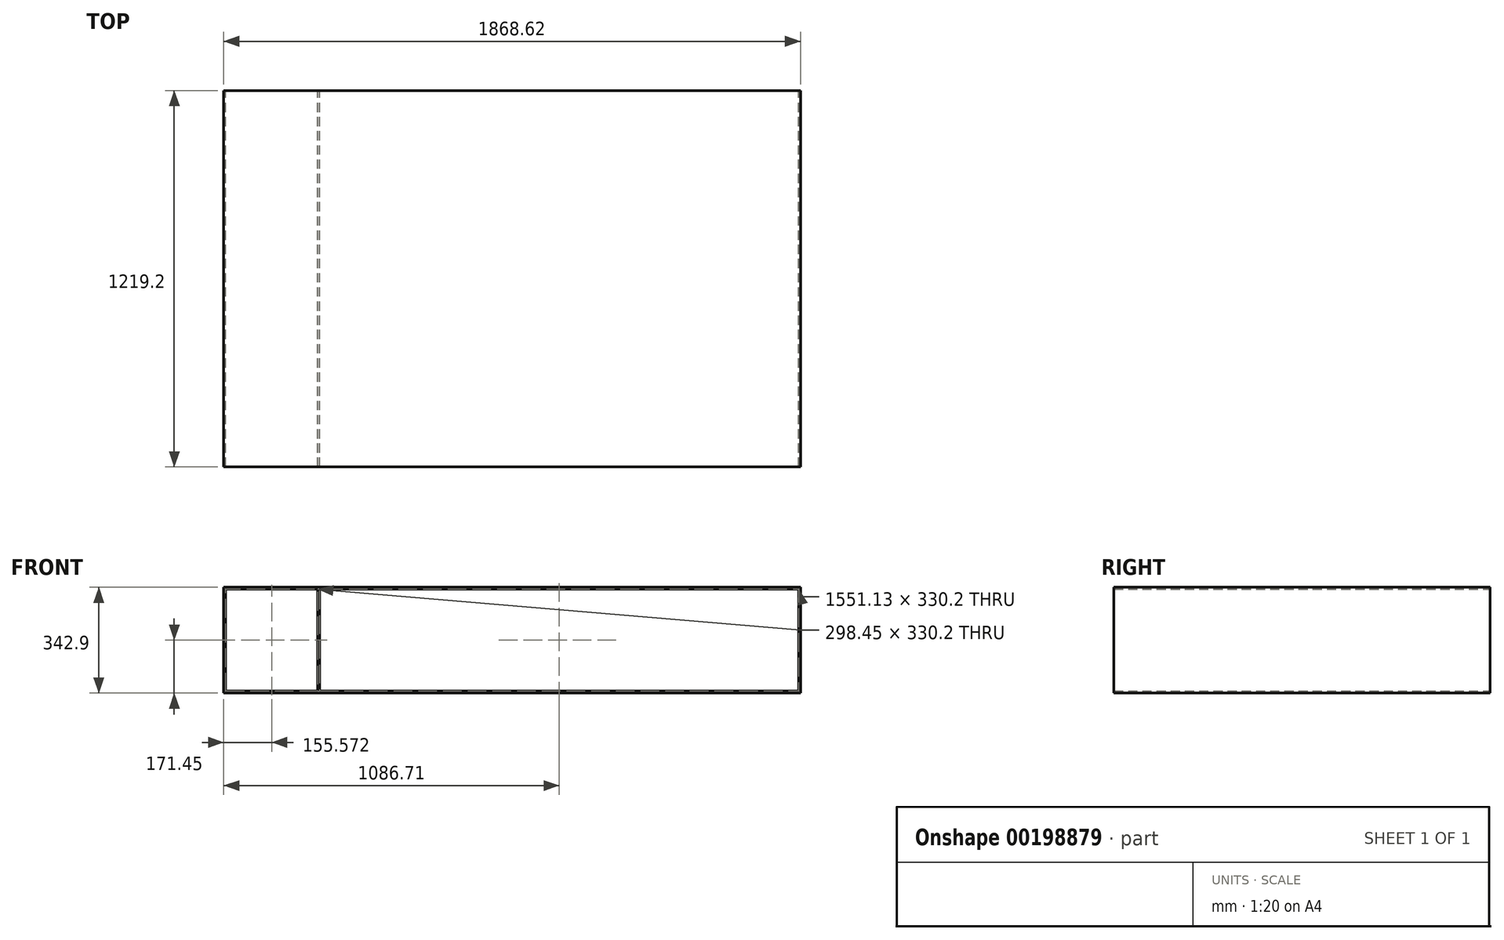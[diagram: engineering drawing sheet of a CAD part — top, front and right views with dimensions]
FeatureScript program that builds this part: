
annotation { "Feature Type Name" : "Feature", "Feature Type Description" : "" }
export const myFeature = defineFeature(function(context is Context, id is Id, definition is map)
    precondition{}
    {
        {
            var Q0;
            Q0=qCreatedBy(makeId("Front.planeOp"),FACE);
            var sketch = newSketch(context, id + "F0", { "sketchPlane" : qUnion([Q0])});
            skLineSegment(sketch, "E0.bottom", {"start": v(-927.96, 0) * mm, "end": v(-629.51, 0) * mm});
            skLineSegment(sketch, "E0.top", {"start": v(-927.96, 330.2) * mm, "end": v(-629.51, 330.2) * mm});
            skLineSegment(sketch, "E0.left", {"start": v(-927.96, 0) * mm, "end": v(-927.96, 330.2) * mm});
            skLineSegment(sketch, "E0.right", {"start": v(927.96, 0) * mm, "end": v(927.96, 330.2) * mm});
            skLineSegment(sketch, "E1.bottom", {"start": v(-934.31, -6.35) * mm, "end": v(934.31, -6.35) * mm});
            skLineSegment(sketch, "E1.top", {"start": v(-934.31, 336.55) * mm, "end": v(934.31, 336.55) * mm});
            skLineSegment(sketch, "E1.left", {"start": v(-934.31, -6.35) * mm, "end": v(-934.31, 336.55) * mm});
            skLineSegment(sketch, "E1.right", {"start": v(934.31, -6.35) * mm, "end": v(934.31, 336.55) * mm});
            skLineSegment(sketch, "E2", {"start": v(0, 336.55) * mm, "end": v(0, 330.2) * mm, "construction": true});
            skLineSegment(sketch, "E3", {"start": v(927.96, 165.1) * mm, "end": v(934.31, 165.1) * mm, "construction": true});
            skLineSegment(sketch, "E4", {"start": v(-629.51, 330.2) * mm, "end": v(-629.51, 0) * mm});
            skLineSegment(sketch, "E5", {"start": v(-623.16, 330.2) * mm, "end": v(-623.16, 0) * mm});
            skLineSegment(sketch, "E6.trimOffspring", {"start": v(-623.16, 330.2) * mm, "end": v(927.96, 330.2) * mm});
            skLineSegment(sketch, "E7.trimOffspring", {"start": v(-623.16, 0) * mm, "end": v(927.96, 0) * mm});
            skSolve(sketch);
        }
        {
            var Q0;
            Q0 = qSketchRegion(id + "F0", true);
            extrude(context, id + "F1", {"entities" : qUnion([Q0]), "depth" : 1219.2 * mm});
        }
    });
